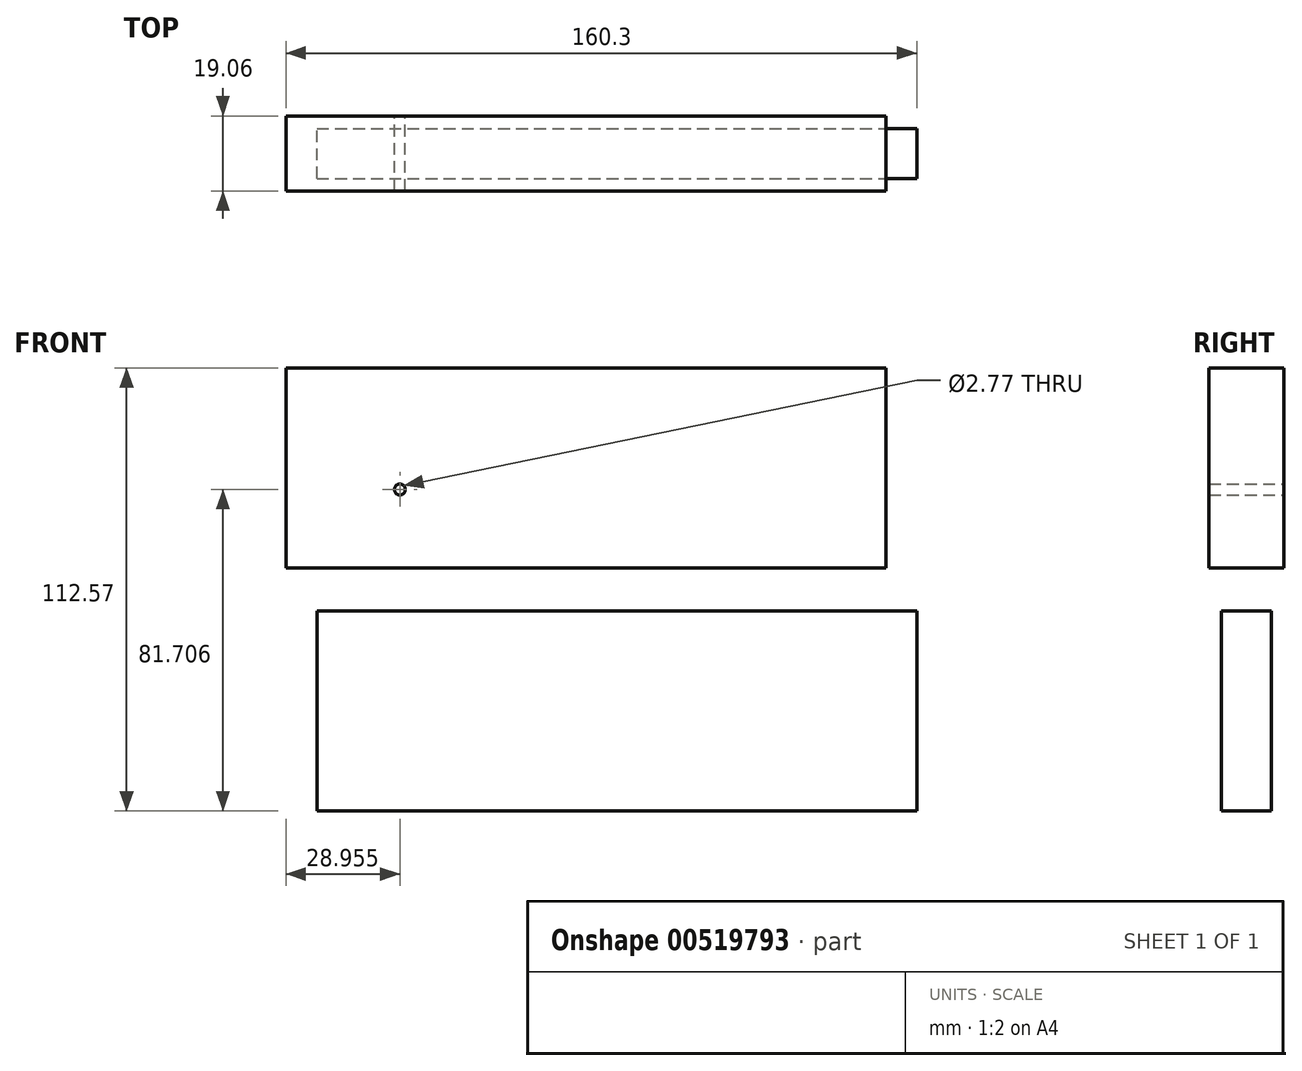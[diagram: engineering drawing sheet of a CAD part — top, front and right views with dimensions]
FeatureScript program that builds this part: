
annotation { "Feature Type Name" : "Feature", "Feature Type Description" : "" }
export const myFeature = defineFeature(function(context is Context, id is Id, definition is map)
    precondition{}
    {
        {
            var Q0;
            Q0=qCreatedBy(makeId("Front.planeOp"),FACE);
            var sketch = newSketch(context, id + "F0", { "sketchPlane" : qUnion([Q0])});
            skLineSegment(sketch, "E0.bottom", {"start": v(-85.45, 25.9) * mm, "end": v(66.95, 25.9) * mm});
            skLineSegment(sketch, "E0.top", {"start": v(-85.45, -24.9) * mm, "end": v(66.95, -24.9) * mm});
            skLineSegment(sketch, "E0.left", {"start": v(-85.45, 25.9) * mm, "end": v(-85.45, -24.9) * mm});
            skLineSegment(sketch, "E0.right", {"start": v(66.95, 25.9) * mm, "end": v(66.95, -24.9) * mm});
            skCircle(sketch, "E1", {"center": v(-56.5, -4.95) * mm, "radius": 1.38 * mm});
            skSolve(sketch);
        }
        {
            var Q0;
            Q0=makeQuery(id+"F0.imprint","IMPRINT",FACE,{"disambiguationData":[TD([[makeQuery(id+"F0.imprint","IMPRINT",EDGE,{"derivedFrom":sQuery(id+"F0.wireOp",EDGE,"E0.bottom")}),-1.0]])]});
            extrude(context, id + "F1", {"entities" : qUnion([Q0]), "endBound" : BoundingType.SYMMETRIC, "depth" : 19.05 * mm, "offsetDistance" : 25.4 * mm});
        }
        {
            var Q0;
            Q0=qCreatedBy(makeId("Front.planeOp"),FACE);
            var sketch = newSketch(context, id + "F2", { "sketchPlane" : qUnion([Q0])});
            skLineSegment(sketch, "E2.bottom", {"start": v(-77.55, -35.86) * mm, "end": v(74.85, -35.86) * mm});
            skLineSegment(sketch, "E2.top", {"start": v(-77.55, -86.66) * mm, "end": v(74.85, -86.66) * mm});
            skLineSegment(sketch, "E2.left", {"start": v(-77.55, -35.86) * mm, "end": v(-77.55, -86.66) * mm});
            skLineSegment(sketch, "E2.right", {"start": v(74.85, -35.86) * mm, "end": v(74.85, -86.66) * mm});
            skSolve(sketch);
        }
        {
            var Q0;
            Q0=makeQuery(id+"F2.imprint","IMPRINT",FACE,{"disambiguationData":[TD([[makeQuery(id+"F2.imprint","IMPRINT",EDGE,{"derivedFrom":sQuery(id+"F2.wireOp",EDGE,"E2.bottom")}),-1.0]])]});
            var Q1;
            Q1=sQuery(id+"F2.wireOp",EDGE,"E2.bottom");
            var Q2;
            Q2=sQuery(id+"F2.wireOp",EDGE,"E2.top");
            var Q3;
            Q3=sQuery(id+"F2.wireOp",EDGE,"E2.left");
            var Q4;
            Q4=sQuery(id+"F2.wireOp",EDGE,"E2.right");
            extrude(context, id + "F3", {"entities" : qUnion([Q0]), "surfaceEntities" : qUnion([Q1, Q2, Q3, Q4]), "endBound" : BoundingType.SYMMETRIC, "depth" : 12.7 * mm, "offsetDistance" : 25.4 * mm});
        }
    });
